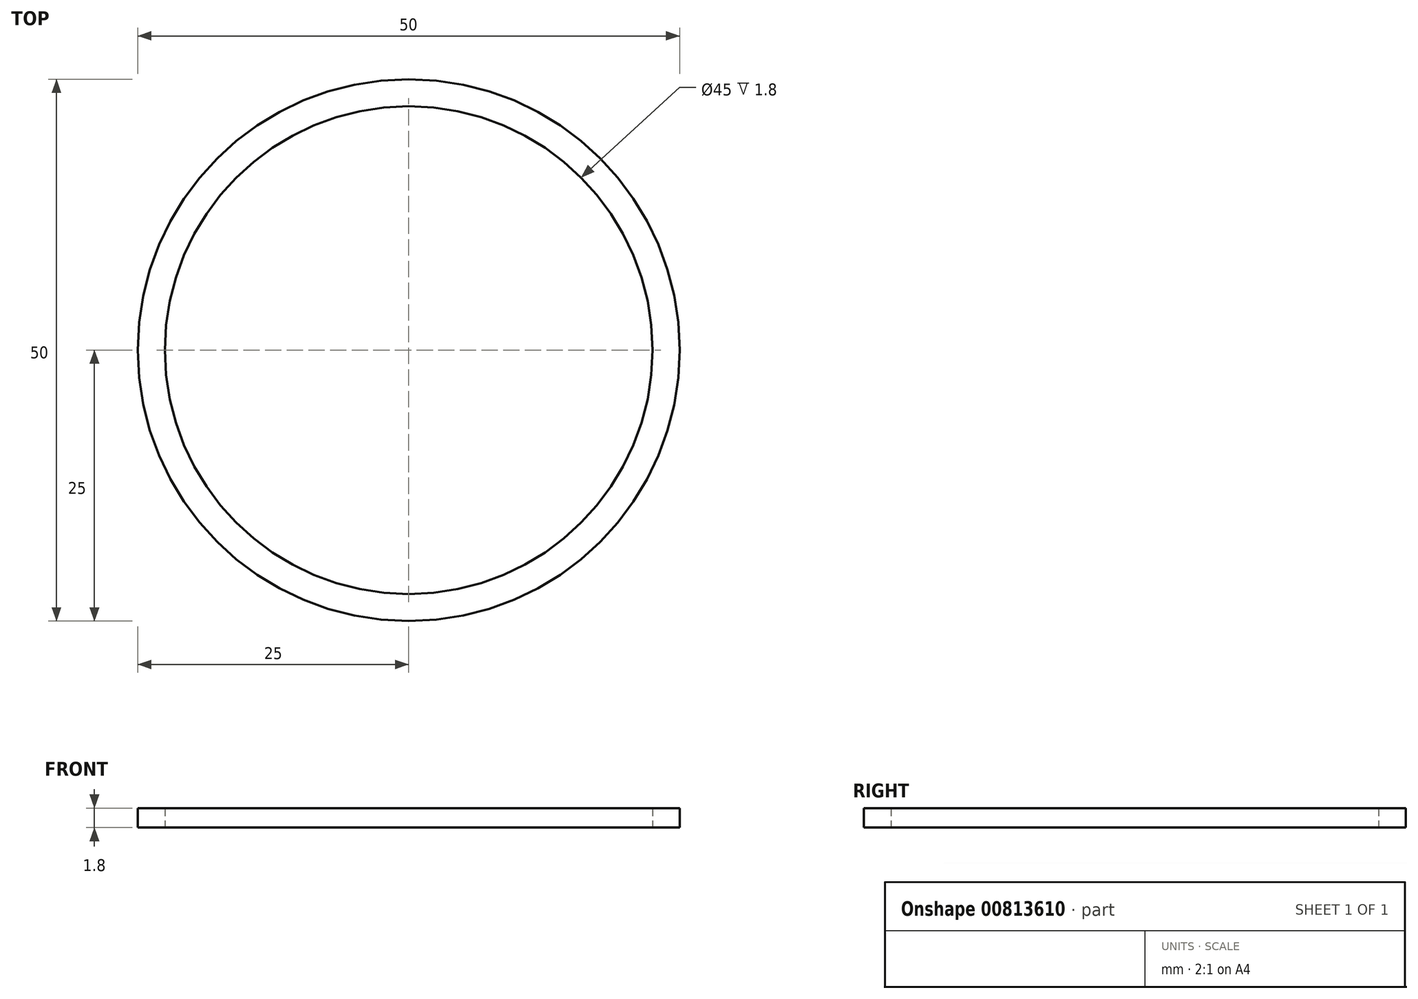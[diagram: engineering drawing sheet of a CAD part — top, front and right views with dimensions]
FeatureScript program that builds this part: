
annotation { "Feature Type Name" : "Feature", "Feature Type Description" : "" }
export const myFeature = defineFeature(function(context is Context, id is Id, definition is map)
    precondition{}
    {
        {
            var Q0;
            Q0=qCreatedBy(makeId("Top.planeOp"),FACE);
            var sketch = newSketch(context, id + "F0", { "sketchPlane" : qUnion([Q0])});
            skCircle(sketch, "E0", {"center": v(0, 0) * mm, "radius": 25 * mm});
            skCircle(sketch, "E1", {"center": v(0, 0) * mm, "radius": 22.5 * mm});
            skSolve(sketch);
        }
        {
            var Q0;
            Q0=makeQuery(id+"F0.imprint","IMPRINT",FACE,{"disambiguationData":[TD([[makeQuery(id+"F0.imprint","IMPRINT",EDGE,{"derivedFrom":sQuery(id+"F0.wireOp",EDGE,"E0")}),1.0]])]});
            extrude(context, id + "F1", {"entities" : qUnion([Q0]), "depth" : 1.8 * mm, "offsetDistance" : 25 * mm});
        }
    });
